# Revit family: ISI_IdealStandard_CounterTopWashbasins_ConceptCube-50cm-Semi
name_source: partatom
category: Plumbing Fixtures
revit_build: Autodesk Revit MEP 2012 (Build: 20110309_2315(x64)
units: mm (PartAtom-declared; Revit-internal decimal feet)

## types (3) — shared parameters
Accessories = www.idealspec.co.uk
AreaUnits = millimeters
Assembly Code = C1030200
AssetType = Fixed
Brand = Ideal Standard
Category = SanitaryTerminal_WASHHANDBASIN_UK
Color = White
ConnectionType = Plumbing
Default Elevation = 1219 mm
DrainSize = 32 mm  [stored 0.104987 ft]
DurationUnit = year
ECA = No
ExpectedLife = 30
Finish = White
IfcExportAs = IfcSanitaryTerminalType
IfcExportType = WASHHANDBASIN
InstallationInstructions = www.idealspec.co.uk/resources.html
LinearUnits = millimeters
ManufacturerURL = www.idealspec.co.uk
Material = Vitreous china
NBSDescription = Counter top washbasins
NBSReference = 45-35-70/360
NettWeight = 12.73 Kg
NominalDepth = 360 mm
NominalHeight = 165 mm
NominalLength = 360 mm
NominalWidth = 500 mm
Shape = Cube
Size = 500 x 360 x 165 mm
Space = Internal
SpareParts = www.fastpart-spares.co.uk
URL = www.idealspec.co.uk
Uniclass2 = Pr_40_20_96_18
Version = 2
VolumeUnits = Litres
WRAS = No
WarrantyDescription = Manufacturers Warranty
WarrantyDurationParts = 99
WarrantyDurationUnit = year
WashHandBasinMounting = CounterTop
WashHandBasinType = HandRinse
WaterEfficientProduct = No
zero-valued in all types: CWFU, HWFU, WFU

## per-type parameters (varying)
| type | 1THLH | 1THRH | 2TH | BIMObjectName | Description | Features | Model | ModelNumber | ModelReference | Name | ProductInformation |
| E779701-Concept Cube 50cm Short Projection Semi-Countertop Washbasin, Glazed Back 2 Tapholes | No | No | Yes | ISI_IdealStandard_CounterTopWashbasins_Concept-Cube-50cm-SemiCounter_E7797 | Concept cube 50 cm short projection semi-countertop washbasin, glazed back 2 tapholes | 50 cm short projection semi countertop washbasin, glazed back edge, 2 tapholes with overflow | E779701 | E779701 | Concept cube 50 cm short projection semi-countertop washbasin, glazed back 2 tapholes | CounterTopWashBasins_Concept-Cube-50cm-SemiCounter_E7797_IdealStandard | www.idealspec.co.uk/assets/datasheet/E779701 |
| E779801-Concept Cube 50cm Short Projection Semi-Countertop Washbasin, Glazed Back 1 LH Taphole | Yes | No | No | ISI_IdealStandard_CounterTopWashbasins_Concept-Cube-50cm-SemiCounter_E7798 | Concept cube 50 cm short projection semi-countertop washbasin, glazed back 1 lh taphole | 50 cm short projection semi countertop washbasin, glazed back edge, 1 left hand taphole with overflow | E779801 | E779801 | Concept cube 50 cm short projection semi-countertop washbasin, glazed back 1 lh taphole | CounterTopWashBasins_Concept-Cube-50cm-SemiCounter_E7798_IdealStandard | www.idealspec.co.uk/assets/datasheet/E779801 |
| E779901-Concept Cube 50cm Short Projection Semi-Countertop Washbasin, Glazed Back 1 RH Taphole | No | Yes | No | ISI_IdealStandard_CounterTopWashbasins_Concept-Cube-50cm-SemiCounter_E7799 | Concept cube 50 cm short projection semi-countertop washbasin, glazed back 1 rh taphole | 50 cm short projection semi countertop washbasin, glazed back edge, 1 right hand taphole with overflow | E779901 | E779901 | Concept cube 50 cm short projection semi-countertop washbasin, glazed back 1 rh taphole | CounterTopWashBasins_Concept-Cube-50cm-SemiCounter_E7799_IdealStandard | www.idealspec.co.uk/assets/datasheet/E779901 |

note: [stored X ft] marks values corroborated as IEEE doubles in the binary element streams (Revit-internal decimal feet)

## geometry (parser evidence)
native form markers: Blend x1, Sweep x7
no freeform markers — native parametric forms only
